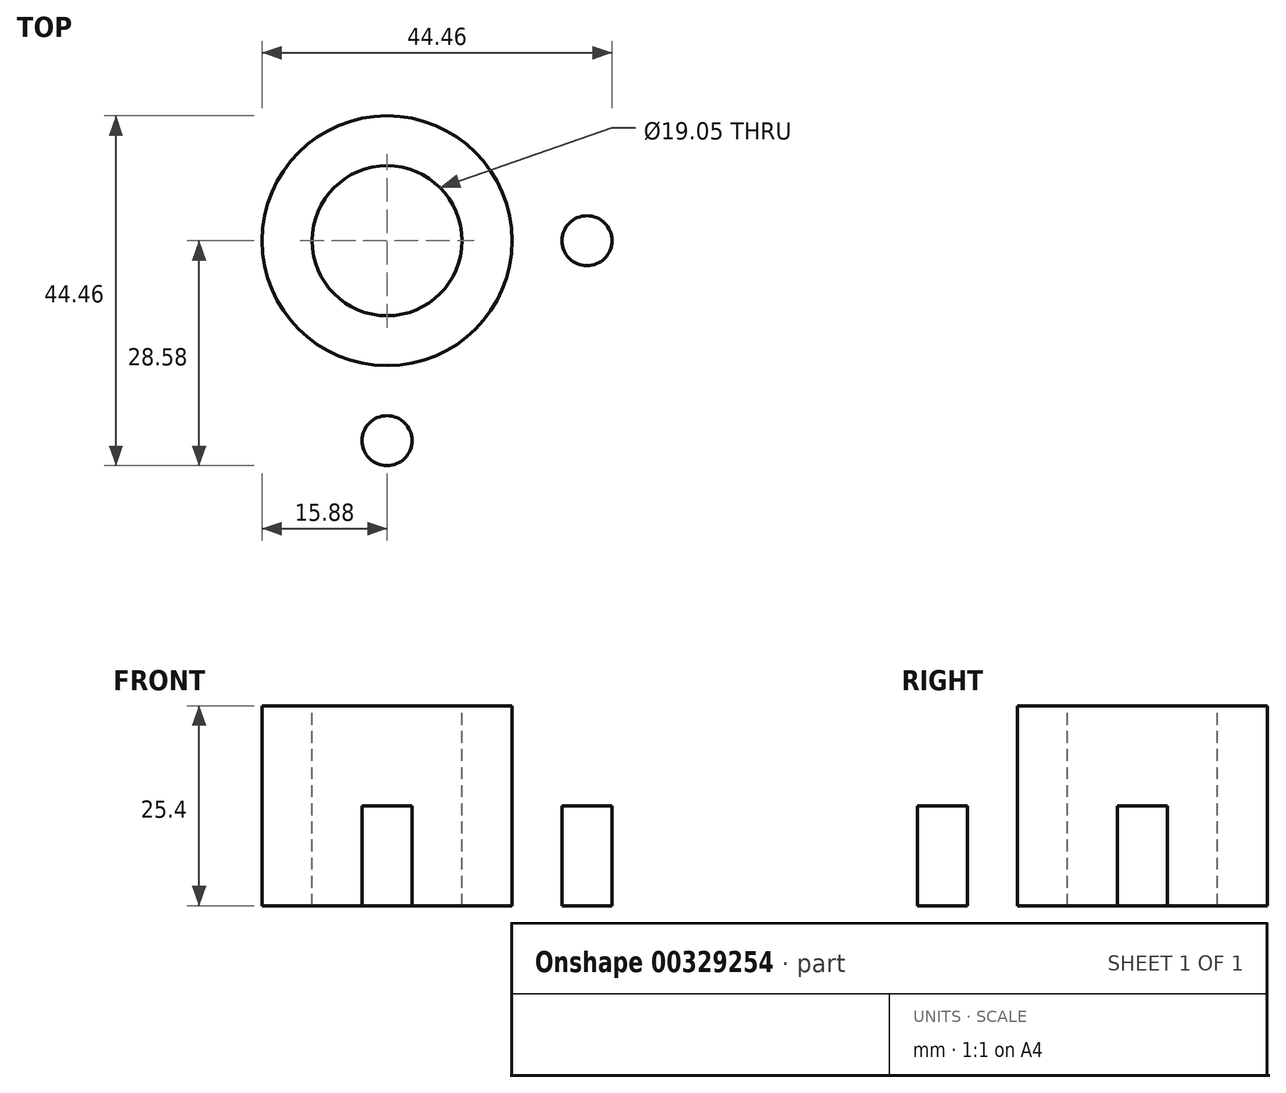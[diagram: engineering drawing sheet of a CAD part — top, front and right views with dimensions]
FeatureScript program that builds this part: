
annotation { "Feature Type Name" : "Feature", "Feature Type Description" : "" }
export const myFeature = defineFeature(function(context is Context, id is Id, definition is map)
    precondition{}
    {
        {
            var Q0;
            Q0=qCreatedBy(makeId("Top.planeOp"),FACE);
            var sketch = newSketch(context, id + "F0", { "sketchPlane" : qUnion([Q0])});
            skCircle(sketch, "E0", {"center": v(0, 0) * mm, "radius": 31.75 * mm});
            skSolve(sketch);
        }
        {
            var Q0;
            Q0 = qSketchRegion(id + "F0", true);
            extrude(context, id + "F1", {"entities" : qUnion([Q0]), "endBound" : BoundingType.SYMMETRIC, "depth" : 12.7 * mm});
        }
        {
            var Q0;
            Q0=makeQuery(id+"F1.opExtrude","CAP_FACE",FACE,{"disambiguationData":[OSD([sQuery(id+"F0.wireOp",EDGE,"E0")])],"isStart":false});
            var sketch = newSketch(context, id + "F2", { "sketchPlane" : qUnion([Q0])});
            skCircle(sketch, "E1", {"center": v(0, 0) * mm, "radius": 15.88 * mm});
            skSolve(sketch);
        }
        {
            var Q0;
            Q0 = qSketchRegion(id + "F2", true);
            extrude(context, id + "F3", {"entities" : qUnion([Q0]), "operationType" : NewBodyOperationType.ADD, "depth" : 12.7 * mm});
        }
        {
            var Q0;
            Q0=makeQuery(id+"F3.opExtrude","CAP_FACE",FACE,{"disambiguationData":[OSD([sQuery(id+"F2.wireOp",EDGE,"E1")])],"isStart":false});
            var sketch = newSketch(context, id + "F4", { "sketchPlane" : qUnion([Q0])});
            skCircle(sketch, "E2", {"center": v(0, 0) * mm, "radius": 9.53 * mm});
            skSolve(sketch);
        }
        {
            var Q0;
            Q0=makeQuery(id+"F4.imprint","IMPRINT",FACE,{"disambiguationData":[TD([[makeQuery(id+"F4.imprint","IMPRINT",EDGE,{"derivedFrom":sQuery(id+"F4.wireOp",EDGE,"E2")}),1.0]])]});
            extrude(context, id + "F5", {"entities" : qUnion([Q0]), "operationType" : NewBodyOperationType.REMOVE, "endBound" : BoundingType.THROUGH_ALL, "oppositeDirection" : true, "depth" : 25.4 * mm});
        }
        {
            var Q0;
            Q0=makeQuery(id+"F1.opExtrude","CAP_FACE",FACE,{"disambiguationData":[OSD([sQuery(id+"F0.wireOp",EDGE,"E0")])],"isStart":false});
            var sketch = newSketch(context, id + "F6", { "sketchPlane" : qUnion([Q0])});
            skLineSegment(sketch, "E3", {"start": v(-21.12, 0) * mm, "end": v(47.74, 0) * mm, "construction": true});
            skCircle(sketch, "E4", {"center": v(0, 25.4) * mm, "radius": 3.17 * mm});
            skCircle(sketch, "E5.MirrorC", {"center": v(0, -25.4) * mm, "radius": 3.17 * mm});
            skLineSegment(sketch, "E6", {"start": v(0, 36.7) * mm, "end": v(0, -49.71) * mm, "construction": true});
            skCircle(sketch, "E7", {"center": v(-25.4, 0) * mm, "radius": 3.18 * mm});
            skCircle(sketch, "E8.MirrorC", {"center": v(25.4, 0) * mm, "radius": 3.18 * mm});
            skSolve(sketch);
        }
        {
            var Q0;
            Q0=makeQuery(id+"F6.imprint","IMPRINT",FACE,{"disambiguationData":[TD([[makeQuery(id+"F6.imprint","IMPRINT",EDGE,{"derivedFrom":sQuery(id+"F6.wireOp",EDGE,"E4")}),1.0]])]});
            var Q1;
            Q1=makeQuery(id+"F6.imprint","IMPRINT",FACE,{"disambiguationData":[TD([[makeQuery(id+"F6.imprint","IMPRINT",EDGE,{"derivedFrom":sQuery(id+"F6.wireOp",EDGE,"E8.MirrorC")}),-1.0]])]});
            var Q2;
            Q2=makeQuery(id+"F6.imprint","IMPRINT",FACE,{"disambiguationData":[TD([[makeQuery(id+"F6.imprint","IMPRINT",EDGE,{"derivedFrom":sQuery(id+"F6.wireOp",EDGE,"E5.MirrorC")}),-1.0]])]});
            var Q3;
            Q3=makeQuery(id+"F6.imprint","IMPRINT",FACE,{"disambiguationData":[TD([[makeQuery(id+"F6.imprint","IMPRINT",EDGE,{"derivedFrom":sQuery(id+"F6.wireOp",EDGE,"E7")}),1.0]])]});
            extrude(context, id + "F7", {"entities" : qUnion([Q0, Q1, Q2, Q3]), "operationType" : NewBodyOperationType.REMOVE, "endBound" : BoundingType.THROUGH_ALL, "oppositeDirection" : true, "depth" : 25.4 * mm});
        }
    });
